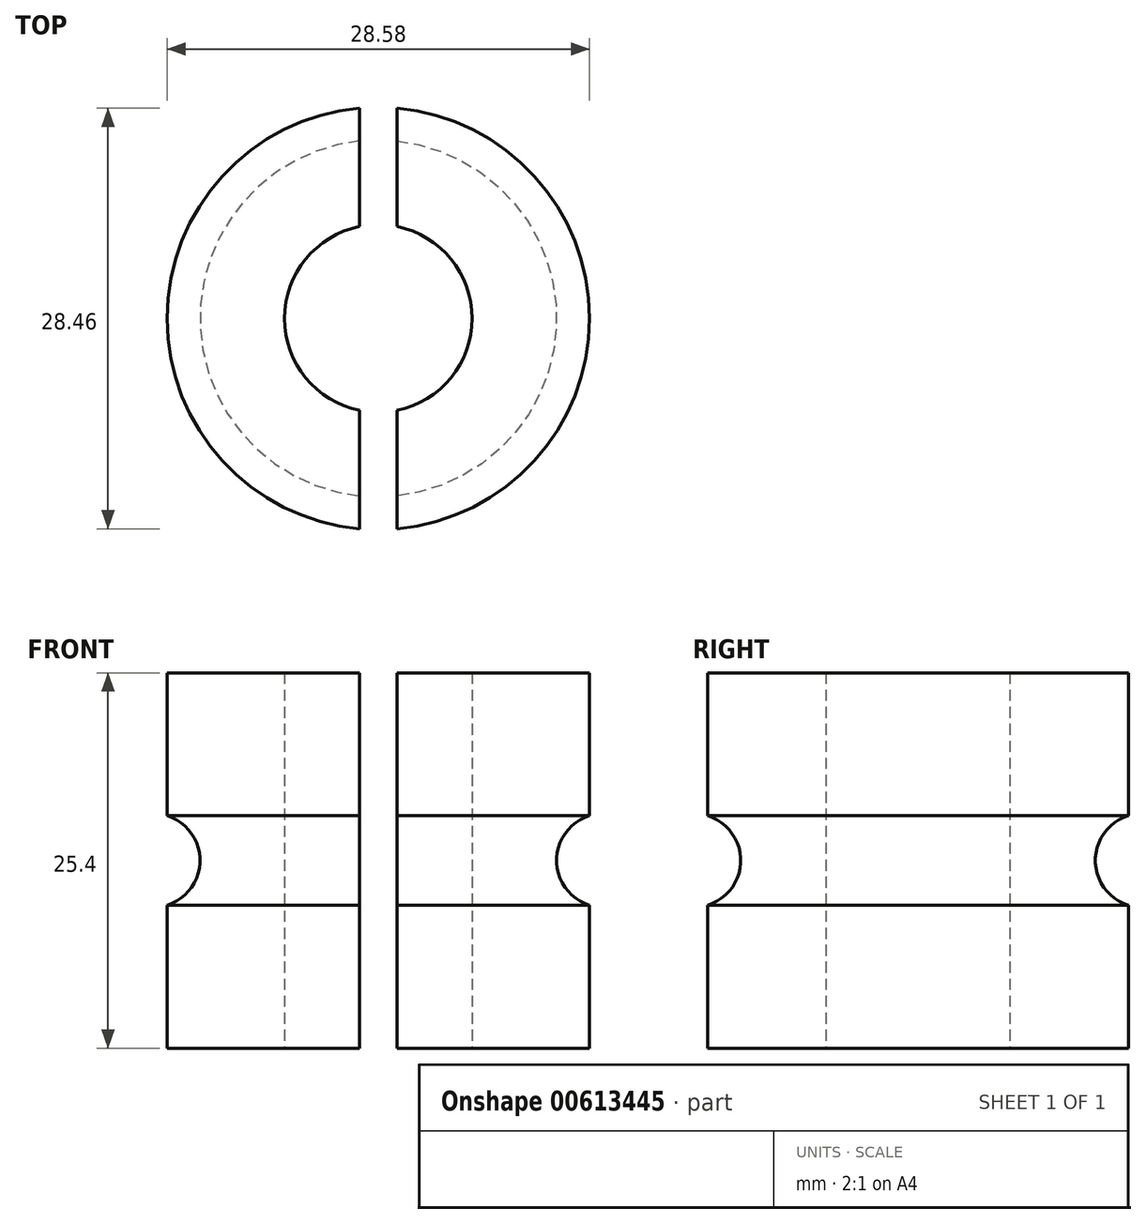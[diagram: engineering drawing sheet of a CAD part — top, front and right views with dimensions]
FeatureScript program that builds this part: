
annotation { "Feature Type Name" : "Feature", "Feature Type Description" : "" }
export const myFeature = defineFeature(function(context is Context, id is Id, definition is map)
    precondition{}
    {
        {
            var Q0;
            Q0=qCreatedBy(makeId("Top.planeOp"),FACE);
            var sketch = newSketch(context, id + "F0", { "sketchPlane" : qUnion([Q0])});
            skCircle(sketch, "E0", {"center": v(0, 0) * mm, "radius": 14.29 * mm});
            skCircle(sketch, "E1", {"center": v(0, 0) * mm, "radius": 6.35 * mm});
            skSolve(sketch);
        }
        {
            var Q0;
            Q0=makeQuery(id+"F0.imprint","IMPRINT",FACE,{"disambiguationData":[TD([[makeQuery(id+"F0.imprint","IMPRINT",EDGE,{"derivedFrom":sQuery(id+"F0.wireOp",EDGE,"E0")}),1.0]])]});
            extrude(context, id + "F1", {"entities" : qUnion([Q0]), "depth" : 25.4 * mm, "offsetDistance" : 25.4 * mm});
        }
        {
            var Q0;
            Q0=qCreatedBy(makeId("Right.planeOp"),FACE);
            var sketch = newSketch(context, id + "F2", { "sketchPlane" : qUnion([Q0])});
            skCircle(sketch, "E2", {"center": v(15.24, 12.7) * mm, "radius": 3.18 * mm});
            skSolve(sketch);
        }
        {
            var Q0;
            Q0 = qSketchRegion(id + "F2", true);
            var Q1;
            Q1=makeQuery(id+"F1.opExtrude","SWEPT_FACE",FACE,{"disambiguationData":[OSD([sQuery(id+"F0.wireOp",EDGE,"E0")])]});
            revolve(context, id + "F3", {"operationType" : NewBodyOperationType.REMOVE, "entities" : qUnion([Q0]), "axis" : qUnion([Q1]), "revolveType" : RevolveType.FULL, "oppositeDirection" : true});
        }
        {
            var Q0;
            Q0=qCreatedBy(makeId("Top.planeOp"),FACE);
            var sketch = newSketch(context, id + "F4", { "sketchPlane" : qUnion([Q0])});
            skLineSegment(sketch, "E3.bottom", {"start": v(-1.27, 15.88) * mm, "end": v(1.27, 15.88) * mm});
            skLineSegment(sketch, "E3.top", {"start": v(-1.27, -15.88) * mm, "end": v(1.27, -15.88) * mm});
            skLineSegment(sketch, "E3.left", {"start": v(-1.27, 15.88) * mm, "end": v(-1.27, -15.88) * mm});
            skLineSegment(sketch, "E3.right", {"start": v(1.27, 15.88) * mm, "end": v(1.27, -15.88) * mm});
            skSolve(sketch);
        }
        {
            var Q0;
            Q0=makeQuery(id+"F4.imprint","IMPRINT",FACE,{"disambiguationData":[TD([[makeQuery(id+"F4.imprint","IMPRINT",EDGE,{"derivedFrom":sQuery(id+"F4.wireOp",EDGE,"E3.bottom")}),-1.0]])]});
            extrude(context, id + "F5", {"entities" : qUnion([Q0]), "operationType" : NewBodyOperationType.REMOVE, "depth" : 25.4 * mm, "offsetDistance" : 25.4 * mm});
        }
    });
